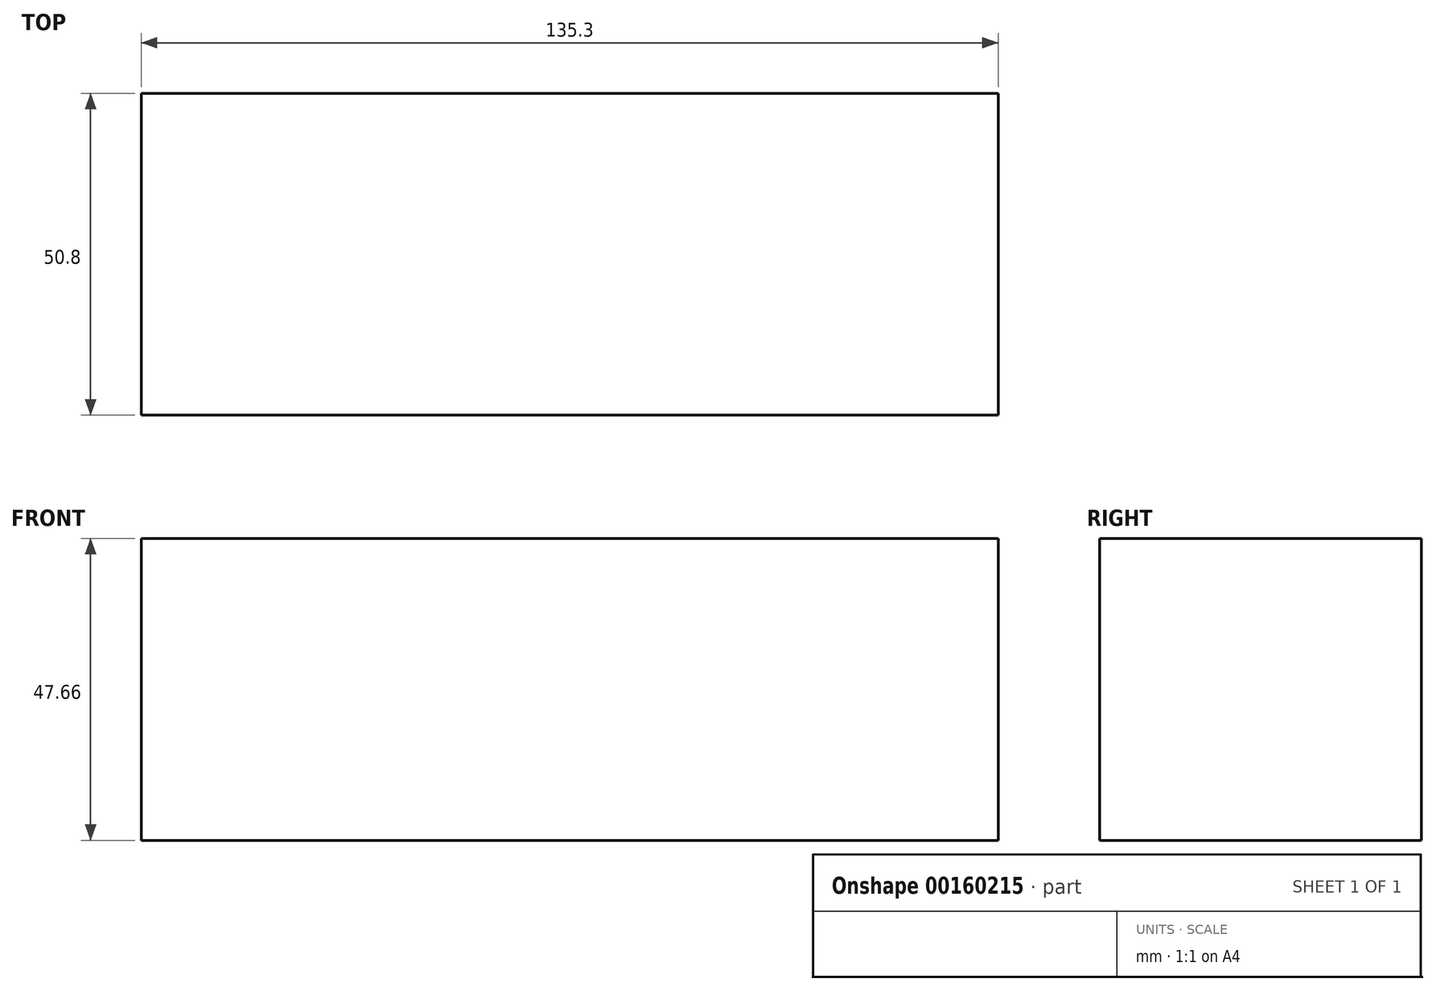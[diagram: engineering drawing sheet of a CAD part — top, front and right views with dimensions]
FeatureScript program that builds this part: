
annotation { "Feature Type Name" : "Feature", "Feature Type Description" : "" }
export const myFeature = defineFeature(function(context is Context, id is Id, definition is map)
    precondition{}
    {
        {
            var Q0;
            Q0=qCreatedBy(makeId("Front.planeOp"),FACE);
            var sketch = newSketch(context, id + "F0", { "sketchPlane" : qUnion([Q0])});
            skLineSegment(sketch, "E0.bottom", {"start": v(67.65, -23.83) * mm, "end": v(-67.65, -23.83) * mm});
            skLineSegment(sketch, "E0.top", {"start": v(67.65, 23.83) * mm, "end": v(-67.65, 23.83) * mm});
            skLineSegment(sketch, "E0.left", {"start": v(67.65, -23.83) * mm, "end": v(67.65, 23.83) * mm});
            skLineSegment(sketch, "E0.right", {"start": v(-67.65, -23.83) * mm, "end": v(-67.65, 23.83) * mm});
            skPoint(sketch, "E0.middle", {"position": v(0, 0) * mm});
            skSolve(sketch);
        }
        {
            var Q0;
            Q0 = qSketchRegion(id + "F0", true);
            extrude(context, id + "F1", {"entities" : qUnion([Q0]), "depth" : 25.4 * mm});
        }
        {
            var Q0;
            Q0=makeQuery(id+"F1.opExtrude","CAP_FACE",FACE,{"disambiguationData":[OSD([sQuery(id+"F0.wireOp",EDGE,"E0.bottom"),sQuery(id+"F0.wireOp",EDGE,"E0.top"),sQuery(id+"F0.wireOp",EDGE,"E0.left"),sQuery(id+"F0.wireOp",EDGE,"E0.right")])],"isStart":false});
            extrude(context, id + "F2", {"entities" : qUnion([Q0]), "operationType" : NewBodyOperationType.ADD, "depth" : 25.4 * mm});
        }
    });
